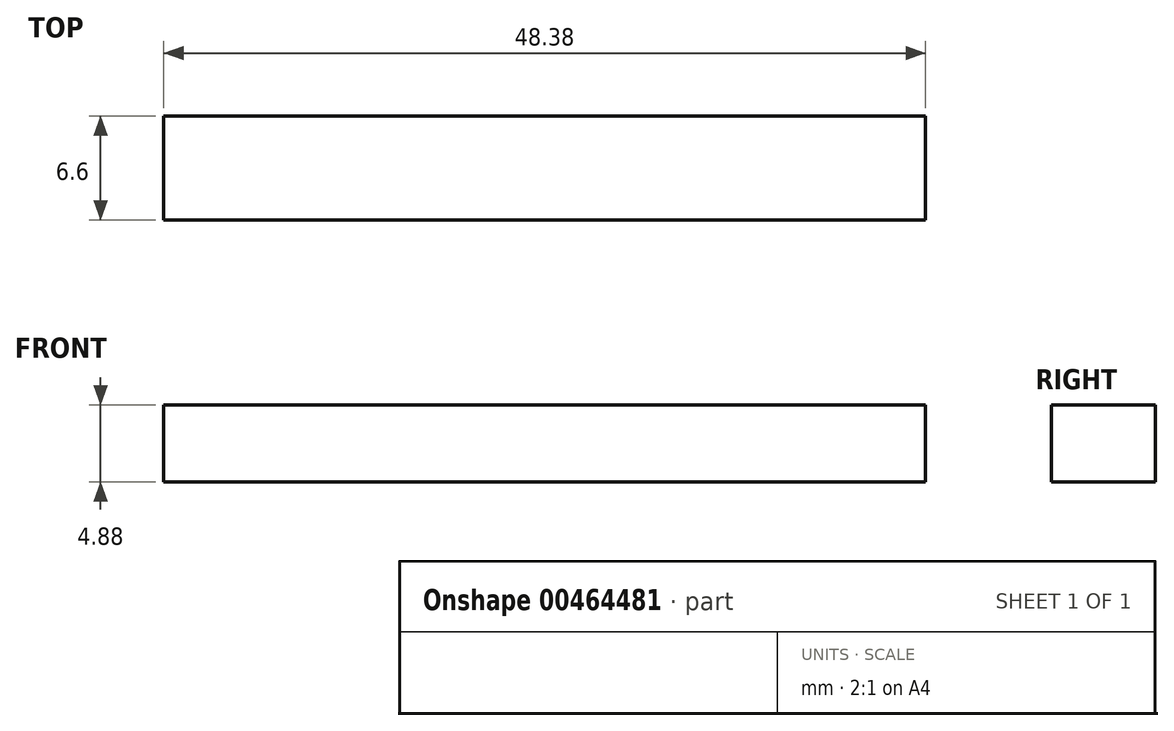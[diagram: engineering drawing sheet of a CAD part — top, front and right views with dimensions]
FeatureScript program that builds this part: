
annotation { "Feature Type Name" : "Feature", "Feature Type Description" : "" }
export const myFeature = defineFeature(function(context is Context, id is Id, definition is map)
    precondition{}
    {
        {
            var Q0;
            Q0=qCreatedBy(makeId("Front.planeOp"),FACE);
            var sketch = newSketch(context, id + "F0", { "sketchPlane" : qUnion([Q0])});
            skLineSegment(sketch, "E0.bottom", {"start": v(-25.12, 13.5) * mm, "end": v(23.26, 13.5) * mm});
            skLineSegment(sketch, "E0.top", {"start": v(-25.12, 8.6) * mm, "end": v(23.26, 8.6) * mm});
            skLineSegment(sketch, "E0.left", {"start": v(-25.12, 13.5) * mm, "end": v(-25.12, 8.6) * mm});
            skLineSegment(sketch, "E0.right", {"start": v(23.26, 13.5) * mm, "end": v(23.26, 8.6) * mm});
            skSolve(sketch);
        }
        {
            var Q0;
            Q0=makeQuery(id+"F0.imprint","IMPRINT",FACE,{"disambiguationData":[TD([[makeQuery(id+"F0.imprint","IMPRINT",EDGE,{"derivedFrom":sQuery(id+"F0.wireOp",EDGE,"E0.bottom")}),-1.0]])]});
            extrude(context, id + "F1", {"entities" : qUnion([Q0]), "depth" : 6.6 * mm});
        }
    });
